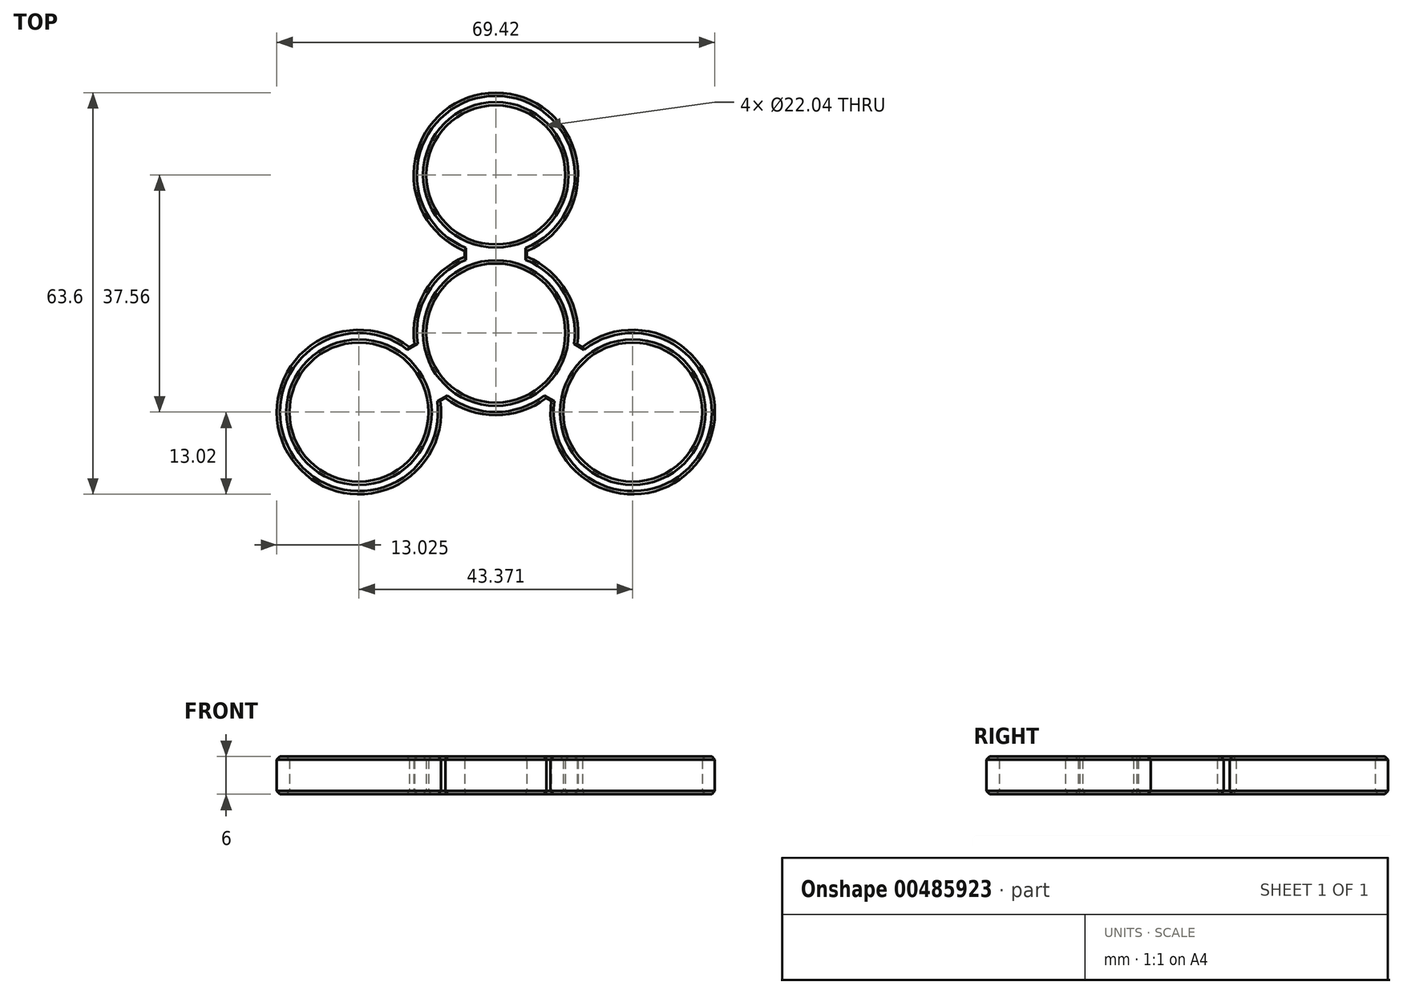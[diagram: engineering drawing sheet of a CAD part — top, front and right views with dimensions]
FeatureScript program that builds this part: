
annotation { "Feature Type Name" : "Feature", "Feature Type Description" : "" }
export const myFeature = defineFeature(function(context is Context, id is Id, definition is map)
    precondition{}
    {
        {
            var Q0;
            Q0=qCreatedBy(makeId("Top.planeOp"),FACE);
            var sketch = newSketch(context, id + "F0", { "sketchPlane" : qUnion([Q0])});
            skCircle(sketch, "E0", {"center": v(0, 0) * mm, "radius": 11.02 * mm});
            skCircle(sketch, "E1", {"center": v(0, 0) * mm, "radius": 25.04 * mm, "construction": true});
            skPoint(sketch, "E2", {"position": v(0, 25.04) * mm});
            skPoint(sketch, "E3", {"position": v(-21.69, -12.52) * mm});
            skPoint(sketch, "E4", {"position": v(21.69, -12.52) * mm});
            skLineSegment(sketch, "E5", {"start": v(0, 0) * mm, "end": v(21.69, -12.52) * mm, "construction": true});
            skLineSegment(sketch, "E6", {"start": v(0, 25.04) * mm, "end": v(0, 0) * mm, "construction": true});
            skLineSegment(sketch, "E7", {"start": v(-21.69, -12.52) * mm, "end": v(0, 0) * mm, "construction": true});
            skCircle(sketch, "E8", {"center": v(0, 25.04) * mm, "radius": 11.02 * mm});
            skCircle(sketch, "E9", {"center": v(-21.69, -12.52) * mm, "radius": 11.02 * mm});
            skCircle(sketch, "E10", {"center": v(21.69, -12.52) * mm, "radius": 11.02 * mm});
            skLineSegment(sketch, "E11", {"start": v(-9.54, -5.5) * mm, "end": v(-12.14, -7) * mm, "construction": true});
            skLineSegment(sketch, "E12", {"start": v(9.54, -5.5) * mm, "end": v(12.14, -7) * mm, "construction": true});
            skLineSegment(sketch, "E13", {"start": v(0, 14.02) * mm, "end": v(0, 11.02) * mm, "construction": true});
            skCircle(sketch, "E14", {"center": v(0, 25.04) * mm, "radius": 13.02 * mm});
            skCircle(sketch, "E15", {"center": v(21.69, -12.52) * mm, "radius": 13.02 * mm});
            skCircle(sketch, "E16", {"center": v(-21.69, -12.52) * mm, "radius": 13.02 * mm});
            skArc(sketch, "E17", {"start": v(-11, 6.97) * mm, "mid": v(-11.28, -6.51) * mm, "end": v(0.54, -13) * mm});
            skArc(sketch, "E18", {"start": v(11, 6.97) * mm, "mid": v(0, 13.02) * mm, "end": v(-11, 6.97) * mm});
            skArc(sketch, "E19", {"start": v(0.54, -13) * mm, "mid": v(11.54, -6.04) * mm, "end": v(11, 6.97) * mm});
            skLineSegment(sketch, "E20", {"start": v(0, 0) * mm, "end": v(-21.69, 12.52) * mm, "construction": true});
            skLineSegment(sketch, "E21", {"start": v(0, 0) * mm, "end": v(21.69, 12.52) * mm, "construction": true});
            skLineSegment(sketch, "E22", {"start": v(0, 0) * mm, "end": v(0, -25.04) * mm, "construction": true});
            skSolve(sketch);
        }
        {
            var Q0;
            Q0=qSketchRegion(id+"F0",true);
            var Q1;
            {var subQ0=sQuery(id+"F0.wireOp",EDGE,"E14");var subQ1=sQuery(id+"F0.wireOp",EDGE,"E0");var subQ2=makeQuery(id+"F0.imprint","INTERSECT",VERTEX,{"disambiguationData":[OD(0.0)],"derivedFrom":[subQ1,subQ0]});Q1=makeQuery(id+"F0.imprint","IMPRINT",FACE,{"disambiguationData":[TD([[makeQuery(id+"F0.imprint","IMPRINT",EDGE,{"disambiguationData":[TD([[subQ2,1.0]])],"derivedFrom":subQ1}),-1.0]])]});}
            var Q2;
            {var subQ0=sQuery(id+"F0.wireOp",EDGE,"E15");var subQ1=sQuery(id+"F0.wireOp",EDGE,"E0");var subQ2=makeQuery(id+"F0.imprint","INTERSECT",VERTEX,{"disambiguationData":[OD(0.0)],"derivedFrom":[subQ1,subQ0]});Q2=makeQuery(id+"F0.imprint","IMPRINT",FACE,{"disambiguationData":[TD([[makeQuery(id+"F0.imprint","IMPRINT",EDGE,{"disambiguationData":[TD([[subQ2,-1.0]])],"derivedFrom":subQ1}),-1.0]])]});}
            var Q3;
            {var subQ0=sQuery(id+"F0.wireOp",EDGE,"E16");var subQ1=sQuery(id+"F0.wireOp",EDGE,"E0");var subQ2=makeQuery(id+"F0.imprint","INTERSECT",VERTEX,{"disambiguationData":[OD(0.0)],"derivedFrom":[subQ1,subQ0]});Q3=makeQuery(id+"F0.imprint","IMPRINT",FACE,{"disambiguationData":[TD([[makeQuery(id+"F0.imprint","IMPRINT",EDGE,{"disambiguationData":[TD([[subQ2,-1.0]])],"derivedFrom":subQ1}),-1.0]])]});}
            var Q4;
            {var subQ4=sQuery(id+"F0.wireOp",EDGE,"iRck3a2y-Tyn7-q6wo-S9O6-DGiwCg7oqTjs");var subQ6=sQuery(id+"F0.wireOp",EDGE,"E8");var subQ7=makeQuery(id+"F0.imprint","INTERSECT",VERTEX,{"disambiguationData":[OD(0.0)],"derivedFrom":[subQ6,subQ4]});Q4=makeQuery(id+"F0.imprint","IMPRINT",FACE,{"disambiguationData":[TD([[makeQuery(id+"F0.imprint","IMPRINT",EDGE,{"disambiguationData":[TD([[subQ7,1.0]])],"derivedFrom":subQ6}),-1.0]])]});}
            var Q5;
            {var subQ4=sQuery(id+"F0.wireOp",EDGE,"iRck3a2y-Tyn7-q6wo-S9O6-DGiwCg7oqTjs");var subQ7=sQuery(id+"F0.wireOp",EDGE,"E9");var subQ8=makeQuery(id+"F0.imprint","INTERSECT",VERTEX,{"disambiguationData":[OD(0.0)],"derivedFrom":[subQ7,subQ4]});Q5=makeQuery(id+"F0.imprint","IMPRINT",FACE,{"disambiguationData":[TD([[makeQuery(id+"F0.imprint","IMPRINT",EDGE,{"disambiguationData":[TD([[subQ8,1.0]])],"derivedFrom":subQ7}),-1.0]])]});}
            var Q6;
            {var subQ4=sQuery(id+"F0.wireOp",EDGE,"iRck3a2y-Tyn7-q6wo-S9O6-DGiwCg7oqTjs");var subQ6=sQuery(id+"F0.wireOp",EDGE,"E10");var subQ7=makeQuery(id+"F0.imprint","INTERSECT",VERTEX,{"disambiguationData":[OD(0.0)],"derivedFrom":[subQ6,subQ4]});Q6=makeQuery(id+"F0.imprint","IMPRINT",FACE,{"disambiguationData":[TD([[makeQuery(id+"F0.imprint","IMPRINT",EDGE,{"disambiguationData":[TD([[subQ7,1.0]])],"derivedFrom":subQ6}),-1.0]])]});}
            var Q7;
            {var subQ2=sQuery(id+"F0.wireOp",EDGE,"E16");var subQ4=sQuery(id+"F0.wireOp",EDGE,"E0");var subQ5=makeQuery(id+"F0.imprint","INTERSECT",VERTEX,{"disambiguationData":[OD(1.0)],"derivedFrom":[subQ4,subQ2]});Q7=makeQuery(id+"F0.imprint","IMPRINT",FACE,{"disambiguationData":[TD([[makeQuery(id+"F0.imprint","IMPRINT",EDGE,{"disambiguationData":[TD([[subQ5,-1.0]])],"derivedFrom":subQ4}),-1.0]])]});}
            var Q8;
            {var subQ4=sQuery(id+"F0.wireOp",EDGE,"E14");var subQ5=sQuery(id+"F0.wireOp",EDGE,"E0");var subQ6=makeQuery(id+"F0.imprint","INTERSECT",VERTEX,{"disambiguationData":[OD(0.0)],"derivedFrom":[subQ5,subQ4]});Q8=makeQuery(id+"F0.imprint","IMPRINT",FACE,{"disambiguationData":[TD([[makeQuery(id+"F0.imprint","IMPRINT",EDGE,{"disambiguationData":[TD([[subQ6,-1.0]])],"derivedFrom":subQ5}),-1.0]])]});}
            var Q9;
            {var subQ3=sQuery(id+"F0.wireOp",EDGE,"E14");var subQ6=sQuery(id+"F0.wireOp",EDGE,"E0");var subQ9=makeQuery(id+"F0.imprint","INTERSECT",VERTEX,{"disambiguationData":[OD(1.0)],"derivedFrom":[subQ6,subQ3]});Q9=makeQuery(id+"F0.imprint","IMPRINT",FACE,{"disambiguationData":[TD([[makeQuery(id+"F0.imprint","IMPRINT",EDGE,{"disambiguationData":[TD([[subQ9,1.0]])],"derivedFrom":subQ6}),-1.0]])]});}
            extrude(context, id + "F1", {"entities" : qUnion([Q0, Q1, Q2, Q3, Q4, Q5, Q6, Q7, Q8, Q9]), "depth" : 6 * mm, "offsetDistance" : 25 * mm});
        }
        {
            var Q0;
            Q0=makeQuery(id+"F1.opExtrude","SWEPT_FACE",FACE,{"disambiguationData":[OSD([sQuery(id+"F0.wireOp",EDGE,"E8")])]});
            var Q1;
            Q1=makeQuery(id+"F1.opExtrude","SWEPT_FACE",FACE,{"disambiguationData":[OSD([sQuery(id+"F0.wireOp",EDGE,"E9")])]});
            var Q2;
            Q2=makeQuery(id+"F1.opExtrude","SWEPT_FACE",FACE,{"disambiguationData":[OSD([sQuery(id+"F0.wireOp",EDGE,"E10")])]});
            var Q3;
            Q3=makeQuery(id+"F1.opExtrude","SWEPT_FACE",FACE,{"disambiguationData":[OSD([sQuery(id+"F0.wireOp",EDGE,"E14")])]});
            var Q4;
            Q4=makeQuery(id+"F1.opExtrude","SWEPT_FACE",FACE,{"disambiguationData":[OSD([sQuery(id+"F0.wireOp",EDGE,"E16")])]});
            var Q5;
            Q5=makeQuery(id+"F1.opExtrude","SWEPT_FACE",FACE,{"disambiguationData":[OSD([sQuery(id+"F0.wireOp",EDGE,"E15")])]});
            var Q6;
            Q6=makeQuery(id+"F1.opExtrude","CAP_EDGE",EDGE,{"disambiguationData":[OSD([sQuery(id+"F0.wireOp",EDGE,"E0")])],"isStart":true});
            var Q7;
            Q7=makeQuery(id+"F1.opExtrude","CAP_EDGE",EDGE,{"disambiguationData":[OSD([sQuery(id+"F0.wireOp",EDGE,"E0")])],"isStart":false});
            chamfer(context, id + "F2", {"entities" : qUnion([Q0, Q1, Q2, Q3, Q4, Q5, Q6, Q7]), "width" : 0.5 * mm, "tangentPropagation" : true});
        }
    });
